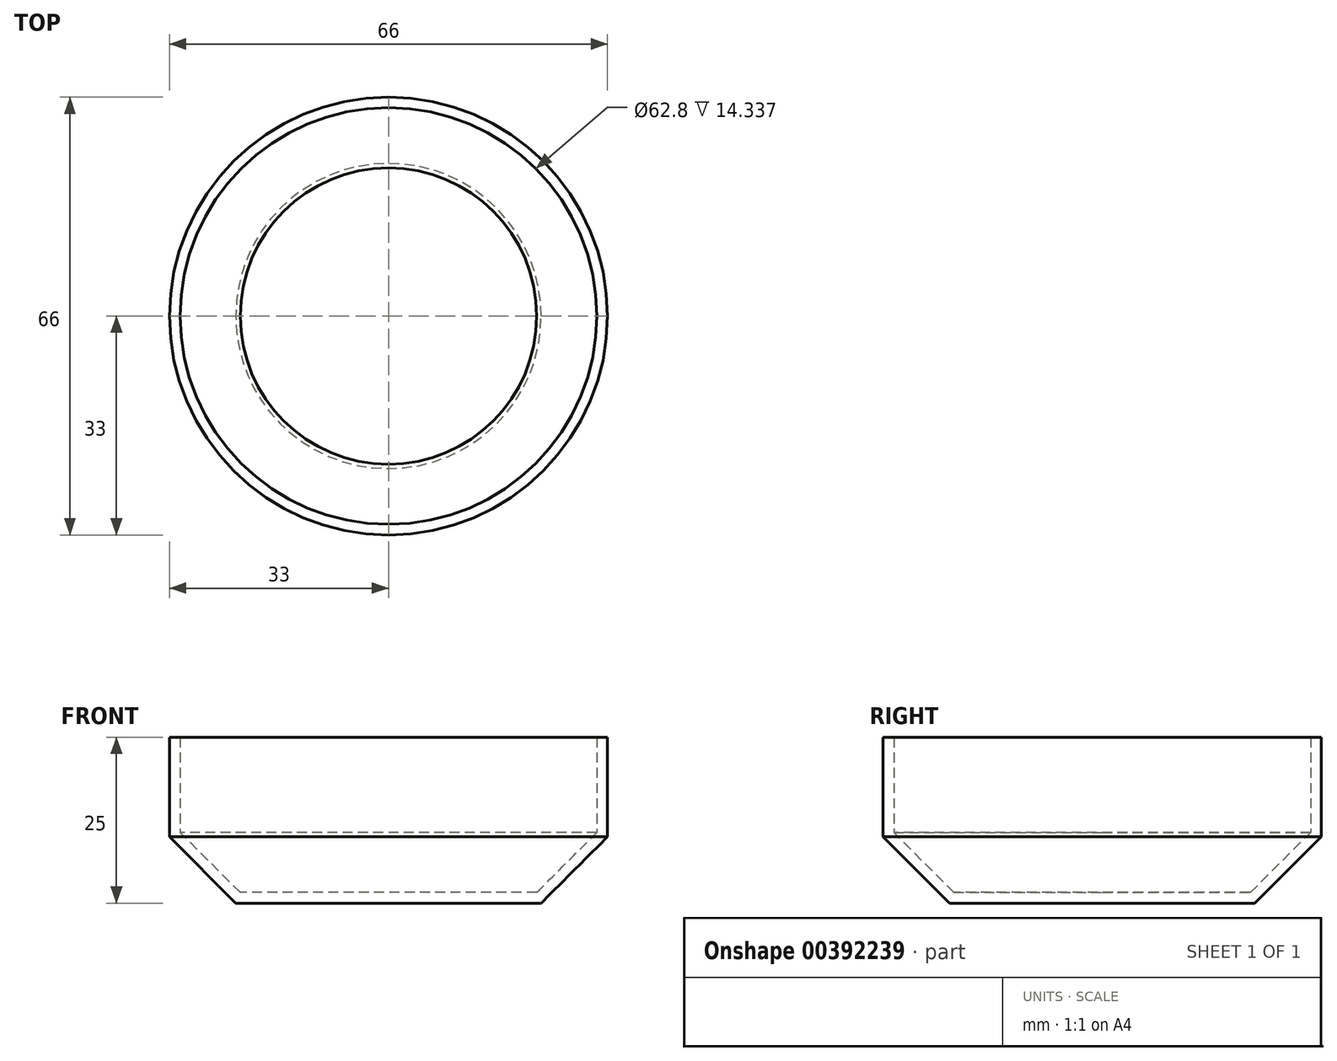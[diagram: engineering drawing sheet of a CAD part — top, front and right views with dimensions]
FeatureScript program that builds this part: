
annotation { "Feature Type Name" : "Feature", "Feature Type Description" : "" }
export const myFeature = defineFeature(function(context is Context, id is Id, definition is map)
    precondition{}
    {
        {
            var Q0;
            Q0=qCreatedBy(makeId("Top.planeOp"),FACE);
            var sketch = newSketch(context, id + "F0", { "sketchPlane" : qUnion([Q0])});
            skCircle(sketch, "E0", {"center": v(0, 0) * mm, "radius": 33 * mm});
            skSolve(sketch);
        }
        {
            var Q0;
            Q0 = qSketchRegion(id + "F0", true);
            extrude(context, id + "F1", {"entities" : qUnion([Q0]), "depth" : 25 * mm});
        }
        {
            var Q0;
            Q0=makeQuery(id+"F1.opExtrude","CAP_EDGE",EDGE,{"disambiguationData":[OSD([sQuery(id+"F0.wireOp",EDGE,"E0")])],"isStart":true});
            chamfer(context, id + "F2", {"entities" : qUnion([Q0]), "width" : 10 * mm, "tangentPropagation" : true});
        }
        {
            var Q0;
            Q0=makeQuery(id+"F1.opExtrude","CAP_FACE",FACE,{"disambiguationData":[OSD([sQuery(id+"F0.wireOp",EDGE,"E0")])],"isStart":false});
            shell(context, id + "F3", {"entities" : qUnion([Q0]), "thickness" : 1.6 * mm});
        }
    });
